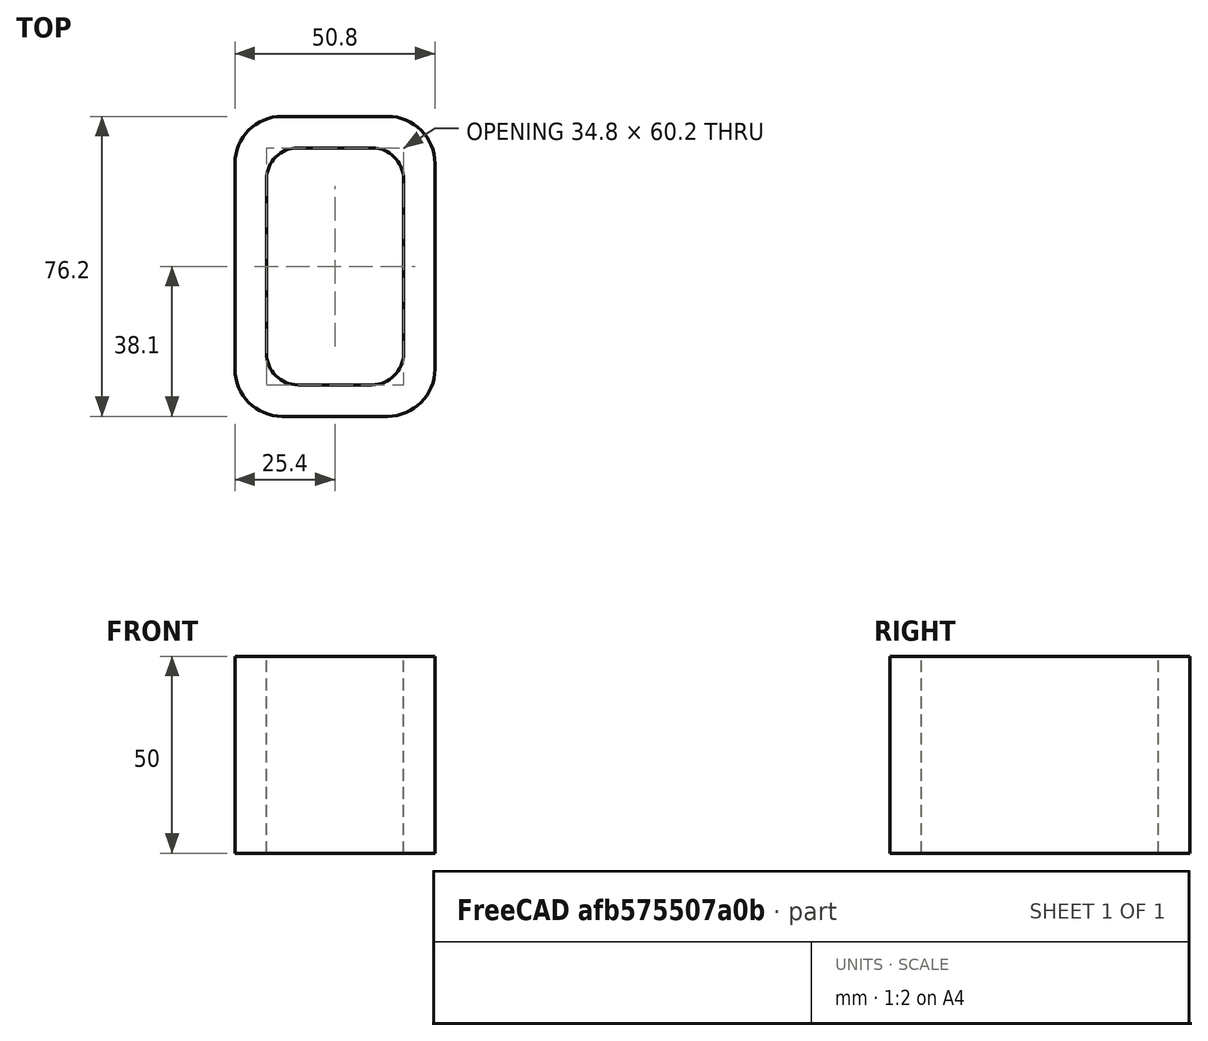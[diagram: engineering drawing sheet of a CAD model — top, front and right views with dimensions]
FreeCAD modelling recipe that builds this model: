
FCSTD DOCUMENT  (FreeCAD 0.15R4671 (Git))
Label: Rectangular hollow section 76.2 x50.8 x8 EN10219 S235JRH
License: All rights reserved
LicenseURL: http://en.wikipedia.org/wiki/All_rights_reserved
objects: Sketcher::SketchObject×1, Part::Extrusion×1
note: 2 computed .brp shape members not serialized (recipe doc carries the construction recipe); baked Part::Feature solids carry a one-line shape summary decoded from their .brp

FEATURE [Sketcher::SketchObject] Sketch
  sketch-geometry (16):
    g0: LineSegment StartX=-9.4 StartY=30.1 StartZ=0 EndX=9.4 EndY=30.1 EndZ=0
    g1: LineSegment StartX=17.4 StartY=22.1 StartZ=0 EndX=17.4 EndY=-22.1 EndZ=0
    g2: LineSegment StartX=9.4 StartY=-30.1 StartZ=0 EndX=-9.4 EndY=-30.1 EndZ=0
    g3: LineSegment StartX=-17.4 StartY=-22.1 StartZ=0 EndX=-17.4 EndY=22.1 EndZ=0
    g4: LineSegment StartX=-13.4 StartY=38.1 StartZ=0 EndX=13.4 EndY=38.1 EndZ=0
    g5: LineSegment StartX=25.4 StartY=26.1 StartZ=0 EndX=25.4 EndY=-26.1 EndZ=0
    g6: LineSegment StartX=13.4 StartY=-38.1 StartZ=0 EndX=-13.4 EndY=-38.1 EndZ=0
    g7: LineSegment StartX=-25.4 StartY=-26.1 StartZ=0 EndX=-25.4 EndY=26.1 EndZ=0
    g8: ArcOfCircle CenterX=-9.4 CenterY=22.1 CenterZ=0 NormalX=0 NormalY=0 NormalZ=1 Radius=8 StartAngle=1.5708 EndAngle=3.14159
    g9: ArcOfCircle CenterX=9.4 CenterY=22.1 CenterZ=0 NormalX=0 NormalY=0 NormalZ=1 Radius=8 StartAngle=0 EndAngle=1.5708
    g10: ArcOfCircle CenterX=9.4 CenterY=-22.1 CenterZ=0 NormalX=0 NormalY=0 NormalZ=1 Radius=8 StartAngle=4.71239 EndAngle=6.28319
    g11: ArcOfCircle CenterX=-9.4 CenterY=-22.1 CenterZ=0 NormalX=0 NormalY=0 NormalZ=1 Radius=8 StartAngle=3.14159 EndAngle=4.71239
    g12: ArcOfCircle CenterX=13.4 CenterY=26.1 CenterZ=0 NormalX=0 NormalY=0 NormalZ=1 Radius=12 StartAngle=0 EndAngle=1.5708
    g13: ArcOfCircle CenterX=13.4 CenterY=-26.1 CenterZ=0 NormalX=0 NormalY=0 NormalZ=1 Radius=12 StartAngle=4.71239 EndAngle=6.28319
    g14: ArcOfCircle CenterX=-13.4 CenterY=-26.1 CenterZ=0 NormalX=0 NormalY=0 NormalZ=1 Radius=12 StartAngle=3.14159 EndAngle=4.71239
    g15: ArcOfCircle CenterX=-13.4 CenterY=26.1 CenterZ=0 NormalX=0 NormalY=0 NormalZ=1 Radius=12 StartAngle=1.5708 EndAngle=3.14159
  constraints (36):
    c: Horizontal(g2)
    c: Vertical(g3)
    c: Horizontal(g6)
    c: Vertical(g7)
    c: Tangent(g3,g8) = 1.5708
    c: Tangent(g0,g8) = 1.5708
    c: Tangent(g0,g9) = 1.5708
    c: Tangent(g1,g9) = 1.5708
    c: Tangent(g1,g10) = 1.5708
    c: Tangent(g2,g10) = 1.5708
    c: Tangent(g2,g11) = 1.5708
    c: Tangent(g3,g11) = 1.5708
    c: Tangent(g4,g12) = 1.5708
    c: Tangent(g5,g12) = 1.5708
    c: Tangent(g5,g13) = 1.5708
    c: Tangent(g6,g13) = 1.5708
    c: Tangent(g6,g14) = 1.5708
    c: Tangent(g7,g14) = 1.5708
    c: Tangent(g7,g15) = 1.5708
    c: Tangent(g4,g15) = 1.5708
    c: Equal(g9,g8)
    c: Equal(g9,g11)
    c: Equal(g9,g10)
    c: Equal(g12,g15)
    c: Equal(g12,g14)
    c: Equal(g12,g13)
    c: Symmetric(g4,g6,g-1)
    c: Symmetric(g7,g5,g-2)
    c: DistanceY(g4,g6) = -76.2
    c: DistanceX(g7,g5) = 50.8
    c: Symmetric(g3,g1,g-2)
    c: Symmetric(g0,g2,g-1)
    c: DistanceY(g0,g4) = 8
    c: DistanceX(g5,g1) = -8
    c: Radius(g9) = 8
    c: Radius(g12) = 12
FEATURE [Part::Extrusion] Extrude  label="Rectangular hollow section 76.2 x50.8 x8 EN10219 S235JRH"
  Base = -> Sketch
  Dir = (0,0,50)
  Solid = true
